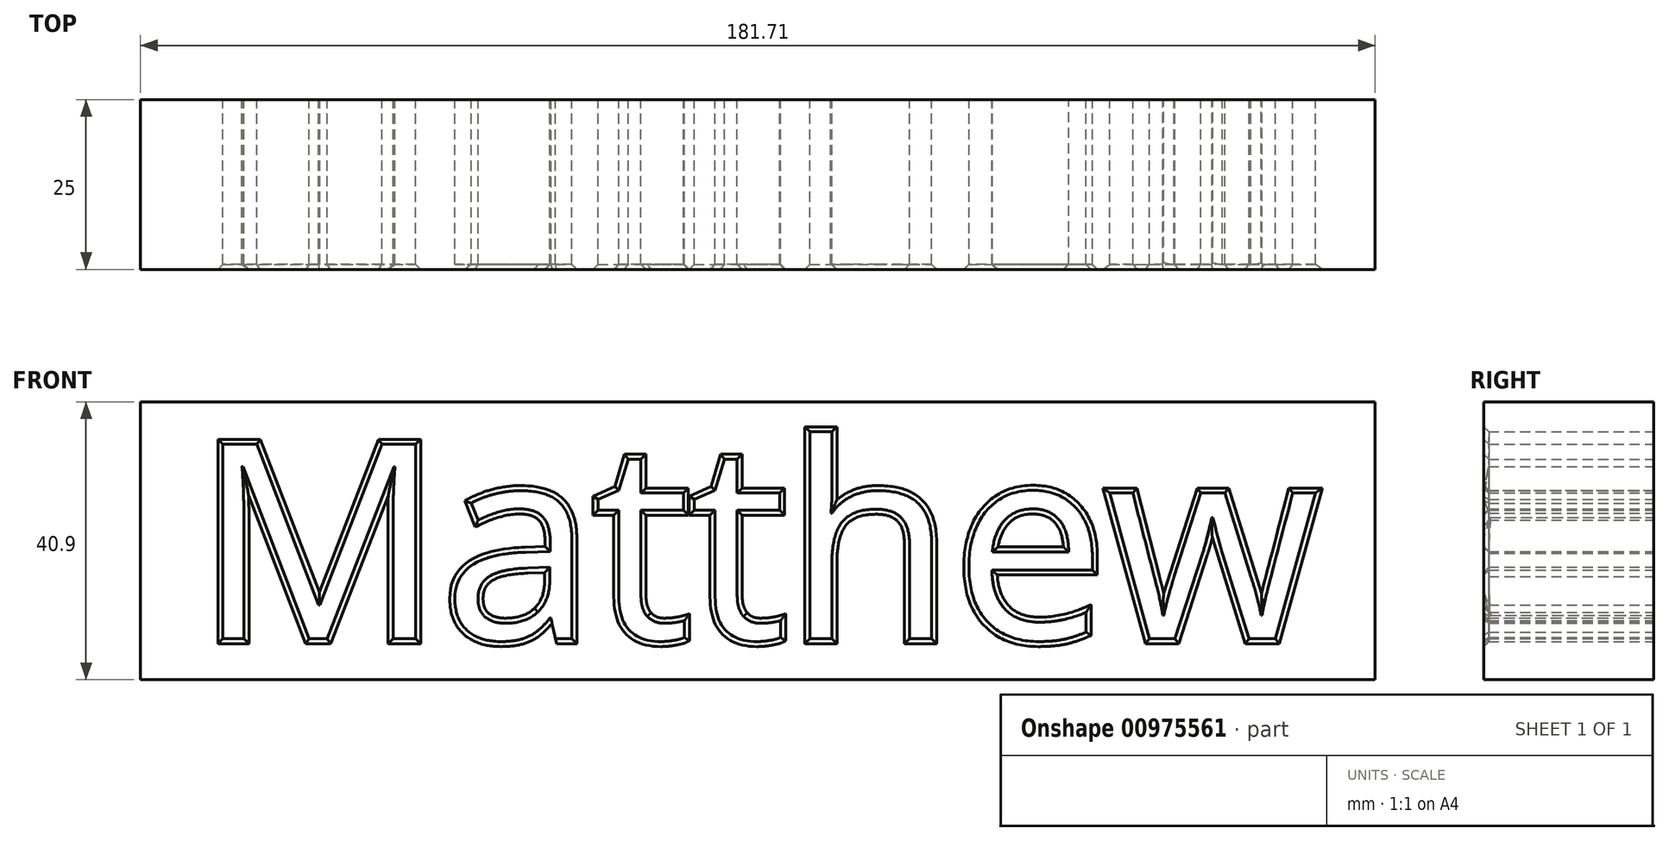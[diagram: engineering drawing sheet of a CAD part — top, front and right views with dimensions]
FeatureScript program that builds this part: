
annotation { "Feature Type Name" : "Feature", "Feature Type Description" : "" }
export const myFeature = defineFeature(function(context is Context, id is Id, definition is map)
    precondition{}
    {
        {
            var Q0;
            Q0=qCreatedBy(makeId("Front.planeOp"),FACE);
            var sketch = newSketch(context, id + "F0", { "sketchPlane" : qUnion([Q0])});
            skLineSegment(sketch, "E0.bottom", {"start": v(-90.14, 64.05) * mm, "end": v(91.57, 64.05) * mm});
            skLineSegment(sketch, "E0.top", {"start": v(-90.14, 23.15) * mm, "end": v(91.57, 23.15) * mm});
            skLineSegment(sketch, "E0.left", {"start": v(-90.14, 64.05) * mm, "end": v(-90.14, 23.15) * mm});
            skLineSegment(sketch, "E0.right", {"start": v(91.57, 64.05) * mm, "end": v(91.57, 23.15) * mm});
            skText(sketch, "E1", { "text": "Matthew", "fontName": "OpenSans-Regular.ttf"});
            const initialGuessF0  = {"E1": [-0.08195, 0.02915, 1, 0, 0.02889]};
            skSetInitialGuess(sketch, initialGuessF0);
            skSolve(sketch);
        }
        {
            var Q0;
            Q0=makeQuery(id+"F0.imprint","IMPRINT",FACE,{"disambiguationData":[TD([[makeQuery(id+"F0.imprint","IMPRINT",EDGE,{"derivedFrom":sQuery(id+"F0.wireOp",EDGE,"E0.bottom")}),-1.0]])]});
            var Q1;
            Q1=makeQuery(id+"F0.imprint","IMPRINT",FACE,{"disambiguationData":[TD([[makeQuery(id+"F0.imprint","IMPRINT",EDGE,{"derivedFrom":sQuery(id+"F0.wireOp",EDGE,"E1.sketch_text.stroke-37")}),1.0]])]});
            var Q2;
            Q2=makeQuery(id+"F0.imprint","IMPRINT",FACE,{"disambiguationData":[TD([[makeQuery(id+"F0.imprint","IMPRINT",EDGE,{"derivedFrom":sQuery(id+"F0.wireOp",EDGE,"E1.sketch_text.stroke-115")}),1.0]])]});
            extrude(context, id + "F1", {"entities" : qUnion([Q0, Q1, Q2]), "depth" : 25 * mm, "offsetDistance" : 25 * mm});
        }
        {
            var Q0;
            Q0=makeQuery(id+"F1.opExtrude","CAP_EDGE",EDGE,{"disambiguationData":[OSD([sQuery(id+"F0.wireOp",EDGE,"E1.sketch_text.stroke-7")])],"isStart":false});
            var Q1;
            Q1=makeQuery(id+"F1.opExtrude","CAP_EDGE",EDGE,{"disambiguationData":[OSD([sQuery(id+"F0.wireOp",EDGE,"E1.sketch_text.stroke-9")])],"isStart":false});
            var Q2;
            Q2=makeQuery(id+"F1.opExtrude","CAP_EDGE",EDGE,{"disambiguationData":[OSD([sQuery(id+"F0.wireOp",EDGE,"E1.sketch_text.stroke-16")])],"isStart":false});
            var Q3;
            Q3=makeQuery(id+"F1.opExtrude","CAP_EDGE",EDGE,{"disambiguationData":[OSD([sQuery(id+"F0.wireOp",EDGE,"E1.sketch_text.stroke-0")])],"isStart":false});
            var Q4;
            Q4=makeQuery(id+"F1.opExtrude","CAP_EDGE",EDGE,{"disambiguationData":[OSD([sQuery(id+"F0.wireOp",EDGE,"E1.sketch_text.stroke-6")])],"isStart":false});
            var Q5;
            Q5=makeQuery(id+"F1.opExtrude","CAP_EDGE",EDGE,{"disambiguationData":[OSD([sQuery(id+"F0.wireOp",EDGE,"E1.sketch_text.stroke-10")])],"isStart":false});
            var Q6;
            Q6=makeQuery(id+"F1.opExtrude","CAP_EDGE",EDGE,{"disambiguationData":[OSD([sQuery(id+"F0.wireOp",EDGE,"E1.sketch_text.stroke-11")])],"isStart":false});
            var Q7;
            Q7=makeQuery(id+"F1.opExtrude","CAP_EDGE",EDGE,{"disambiguationData":[OSD([sQuery(id+"F0.wireOp",EDGE,"E1.sketch_text.stroke-13")])],"isStart":false});
            var Q8;
            Q8=makeQuery(id+"F1.opExtrude","CAP_EDGE",EDGE,{"disambiguationData":[OSD([sQuery(id+"F0.wireOp",EDGE,"E1.sketch_text.stroke-3")])],"isStart":false});
            var Q9;
            Q9=makeQuery(id+"F1.opExtrude","CAP_EDGE",EDGE,{"disambiguationData":[OSD([sQuery(id+"F0.wireOp",EDGE,"E1.sketch_text.stroke-5")])],"isStart":false});
            var Q10;
            Q10=makeQuery(id+"F1.opExtrude","CAP_EDGE",EDGE,{"disambiguationData":[OSD([sQuery(id+"F0.wireOp",EDGE,"E1.sketch_text.stroke-2")])],"isStart":false});
            var Q11;
            Q11=makeQuery(id+"F1.opExtrude","CAP_EDGE",EDGE,{"disambiguationData":[OSD([sQuery(id+"F0.wireOp",EDGE,"E1.sketch_text.stroke-17")])],"isStart":false});
            var Q12;
            Q12=makeQuery(id+"F1.opExtrude","CAP_EDGE",EDGE,{"disambiguationData":[OSD([sQuery(id+"F0.wireOp",EDGE,"E1.sketch_text.stroke-4")])],"isStart":false});
            var Q13;
            Q13=makeQuery(id+"F1.opExtrude","CAP_EDGE",EDGE,{"disambiguationData":[OSD([sQuery(id+"F0.wireOp",EDGE,"E1.sketch_text.stroke-12")])],"isStart":false});
            var Q14;
            Q14=makeQuery(id+"F1.opExtrude","CAP_EDGE",EDGE,{"disambiguationData":[OSD([sQuery(id+"F0.wireOp",EDGE,"E1.sketch_text.stroke-14")])],"isStart":false});
            var Q15;
            Q15=makeQuery(id+"F1.opExtrude","CAP_EDGE",EDGE,{"disambiguationData":[OSD([sQuery(id+"F0.wireOp",EDGE,"E1.sketch_text.stroke-33")])],"isStart":false});
            var Q16;
            Q16=makeQuery(id+"F1.opExtrude","CAP_EDGE",EDGE,{"disambiguationData":[OSD([sQuery(id+"F0.wireOp",EDGE,"E1.sketch_text.stroke-24")])],"isStart":false});
            var Q17;
            Q17=makeQuery(id+"F1.opExtrude","CAP_EDGE",EDGE,{"disambiguationData":[OSD([sQuery(id+"F0.wireOp",EDGE,"E1.sketch_text.stroke-29")])],"isStart":false});
            var Q18;
            Q18=makeQuery(id+"F1.opExtrude","CAP_EDGE",EDGE,{"disambiguationData":[OSD([sQuery(id+"F0.wireOp",EDGE,"E1.sketch_text.stroke-30")])],"isStart":false});
            var Q19;
            Q19=makeQuery(id+"F1.opExtrude","CAP_EDGE",EDGE,{"disambiguationData":[OSD([sQuery(id+"F0.wireOp",EDGE,"E1.sketch_text.stroke-36")])],"isStart":false});
            var Q20;
            Q20=makeQuery(id+"F1.opExtrude","CAP_EDGE",EDGE,{"disambiguationData":[OSD([sQuery(id+"F0.wireOp",EDGE,"E1.sketch_text.stroke-41")])],"isStart":false});
            var Q21;
            Q21=makeQuery(id+"F1.opExtrude","CAP_EDGE",EDGE,{"disambiguationData":[OSD([sQuery(id+"F0.wireOp",EDGE,"E1.sketch_text.stroke-55")])],"isStart":false});
            var Q22;
            Q22=makeQuery(id+"F1.opExtrude","CAP_EDGE",EDGE,{"disambiguationData":[OSD([sQuery(id+"F0.wireOp",EDGE,"E1.sketch_text.stroke-56")])],"isStart":false});
            var Q23;
            Q23=makeQuery(id+"F1.opExtrude","CAP_EDGE",EDGE,{"disambiguationData":[OSD([sQuery(id+"F0.wireOp",EDGE,"E1.sketch_text.stroke-57")])],"isStart":false});
            var Q24;
            Q24=makeQuery(id+"F1.opExtrude","CAP_EDGE",EDGE,{"disambiguationData":[OSD([sQuery(id+"F0.wireOp",EDGE,"E1.sketch_text.stroke-58")])],"isStart":false});
            var Q25;
            Q25=makeQuery(id+"F1.opExtrude","CAP_EDGE",EDGE,{"disambiguationData":[OSD([sQuery(id+"F0.wireOp",EDGE,"E1.sketch_text.stroke-60")])],"isStart":false});
            var Q26;
            Q26=makeQuery(id+"F1.opExtrude","CAP_EDGE",EDGE,{"disambiguationData":[OSD([sQuery(id+"F0.wireOp",EDGE,"E1.sketch_text.stroke-59")])],"isStart":false});
            var Q27;
            Q27=makeQuery(id+"F1.opExtrude","CAP_EDGE",EDGE,{"disambiguationData":[OSD([sQuery(id+"F0.wireOp",EDGE,"E1.sketch_text.stroke-53")])],"isStart":false});
            var Q28;
            Q28=makeQuery(id+"F1.opExtrude","CAP_EDGE",EDGE,{"disambiguationData":[OSD([sQuery(id+"F0.wireOp",EDGE,"E1.sketch_text.stroke-54")])],"isStart":false});
            var Q29;
            Q29=makeQuery(id+"F1.opExtrude","CAP_EDGE",EDGE,{"disambiguationData":[OSD([sQuery(id+"F0.wireOp",EDGE,"E1.sketch_text.stroke-51")])],"isStart":false});
            var Q30;
            Q30=makeQuery(id+"F1.opExtrude","CAP_EDGE",EDGE,{"disambiguationData":[OSD([sQuery(id+"F0.wireOp",EDGE,"E1.sketch_text.stroke-52")])],"isStart":false});
            var Q31;
            Q31=makeQuery(id+"F1.opExtrude","CAP_EDGE",EDGE,{"disambiguationData":[OSD([sQuery(id+"F0.wireOp",EDGE,"E1.sketch_text.stroke-63")])],"isStart":false});
            var Q32;
            Q32=makeQuery(id+"F1.opExtrude","CAP_EDGE",EDGE,{"disambiguationData":[OSD([sQuery(id+"F0.wireOp",EDGE,"E1.sketch_text.stroke-47")])],"isStart":false});
            var Q33;
            Q33=makeQuery(id+"F1.opExtrude","CAP_EDGE",EDGE,{"disambiguationData":[OSD([sQuery(id+"F0.wireOp",EDGE,"E1.sketch_text.stroke-72")])],"isStart":false});
            var Q34;
            Q34=makeQuery(id+"F1.opExtrude","CAP_EDGE",EDGE,{"disambiguationData":[OSD([sQuery(id+"F0.wireOp",EDGE,"E1.sketch_text.stroke-73")])],"isStart":false});
            var Q35;
            Q35=makeQuery(id+"F1.opExtrude","CAP_EDGE",EDGE,{"disambiguationData":[OSD([sQuery(id+"F0.wireOp",EDGE,"E1.sketch_text.stroke-71")])],"isStart":false});
            var Q36;
            Q36=makeQuery(id+"F1.opExtrude","CAP_EDGE",EDGE,{"disambiguationData":[OSD([sQuery(id+"F0.wireOp",EDGE,"E1.sketch_text.stroke-70")])],"isStart":false});
            var Q37;
            Q37=makeQuery(id+"F1.opExtrude","CAP_EDGE",EDGE,{"disambiguationData":[OSD([sQuery(id+"F0.wireOp",EDGE,"E1.sketch_text.stroke-80")])],"isStart":false});
            var Q38;
            Q38=makeQuery(id+"F1.opExtrude","CAP_EDGE",EDGE,{"disambiguationData":[OSD([sQuery(id+"F0.wireOp",EDGE,"E1.sketch_text.stroke-66")])],"isStart":false});
            var Q39;
            Q39=makeQuery(id+"F1.opExtrude","CAP_EDGE",EDGE,{"disambiguationData":[OSD([sQuery(id+"F0.wireOp",EDGE,"E1.sketch_text.stroke-79")])],"isStart":false});
            var Q40;
            Q40=makeQuery(id+"F1.opExtrude","CAP_EDGE",EDGE,{"disambiguationData":[OSD([sQuery(id+"F0.wireOp",EDGE,"E1.sketch_text.stroke-78")])],"isStart":false});
            var Q41;
            Q41=makeQuery(id+"F1.opExtrude","CAP_EDGE",EDGE,{"disambiguationData":[OSD([sQuery(id+"F0.wireOp",EDGE,"E1.sketch_text.stroke-77")])],"isStart":false});
            var Q42;
            Q42=makeQuery(id+"F1.opExtrude","CAP_EDGE",EDGE,{"disambiguationData":[OSD([sQuery(id+"F0.wireOp",EDGE,"E1.sketch_text.stroke-76")])],"isStart":false});
            var Q43;
            Q43=makeQuery(id+"F1.opExtrude","CAP_EDGE",EDGE,{"disambiguationData":[OSD([sQuery(id+"F0.wireOp",EDGE,"E1.sketch_text.stroke-75")])],"isStart":false});
            var Q44;
            Q44=makeQuery(id+"F1.opExtrude","CAP_EDGE",EDGE,{"disambiguationData":[OSD([sQuery(id+"F0.wireOp",EDGE,"E1.sketch_text.stroke-74")])],"isStart":false});
            var Q45;
            Q45=makeQuery(id+"F1.opExtrude","CAP_EDGE",EDGE,{"disambiguationData":[OSD([sQuery(id+"F0.wireOp",EDGE,"E1.sketch_text.stroke-92")])],"isStart":false});
            var Q46;
            Q46=makeQuery(id+"F1.opExtrude","CAP_EDGE",EDGE,{"disambiguationData":[OSD([sQuery(id+"F0.wireOp",EDGE,"E1.sketch_text.stroke-93")])],"isStart":false});
            var Q47;
            Q47=makeQuery(id+"F1.opExtrude","CAP_EDGE",EDGE,{"disambiguationData":[OSD([sQuery(id+"F0.wireOp",EDGE,"E1.sketch_text.stroke-96")])],"isStart":false});
            var Q48;
            Q48=makeQuery(id+"F1.opExtrude","CAP_EDGE",EDGE,{"disambiguationData":[OSD([sQuery(id+"F0.wireOp",EDGE,"E1.sketch_text.stroke-100")])],"isStart":false});
            var Q49;
            Q49=makeQuery(id+"F1.opExtrude","CAP_EDGE",EDGE,{"disambiguationData":[OSD([sQuery(id+"F0.wireOp",EDGE,"E1.sketch_text.stroke-83")])],"isStart":false});
            var Q50;
            Q50=makeQuery(id+"F1.opExtrude","CAP_EDGE",EDGE,{"disambiguationData":[OSD([sQuery(id+"F0.wireOp",EDGE,"E1.sketch_text.stroke-89")])],"isStart":false});
            var Q51;
            Q51=makeQuery(id+"F1.opExtrude","CAP_EDGE",EDGE,{"disambiguationData":[OSD([sQuery(id+"F0.wireOp",EDGE,"E1.sketch_text.stroke-91")])],"isStart":false});
            var Q52;
            Q52=makeQuery(id+"F1.opExtrude","CAP_EDGE",EDGE,{"disambiguationData":[OSD([sQuery(id+"F0.wireOp",EDGE,"E1.sketch_text.stroke-90")])],"isStart":false});
            var Q53;
            Q53=makeQuery(id+"F1.opExtrude","CAP_EDGE",EDGE,{"disambiguationData":[OSD([sQuery(id+"F0.wireOp",EDGE,"E1.sketch_text.stroke-103")])],"isStart":false});
            var Q54;
            Q54=makeQuery(id+"F1.opExtrude","CAP_EDGE",EDGE,{"disambiguationData":[OSD([sQuery(id+"F0.wireOp",EDGE,"E1.sketch_text.stroke-108")])],"isStart":false});
            var Q55;
            Q55=makeQuery(id+"F1.opExtrude","CAP_EDGE",EDGE,{"disambiguationData":[OSD([sQuery(id+"F0.wireOp",EDGE,"E1.sketch_text.stroke-111")])],"isStart":false});
            var Q56;
            Q56=makeQuery(id+"F1.opExtrude","CAP_EDGE",EDGE,{"disambiguationData":[OSD([sQuery(id+"F0.wireOp",EDGE,"E1.sketch_text.stroke-112")])],"isStart":false});
            var Q57;
            Q57=makeQuery(id+"F1.opExtrude","CAP_EDGE",EDGE,{"disambiguationData":[OSD([sQuery(id+"F0.wireOp",EDGE,"E1.sketch_text.stroke-117")])],"isStart":false});
            var Q58;
            Q58=makeQuery(id+"F1.opExtrude","CAP_EDGE",EDGE,{"disambiguationData":[OSD([sQuery(id+"F0.wireOp",EDGE,"E1.sketch_text.stroke-119")])],"isStart":false});
            var Q59;
            Q59=makeQuery(id+"F1.opExtrude","CAP_EDGE",EDGE,{"disambiguationData":[OSD([sQuery(id+"F0.wireOp",EDGE,"E1.sketch_text.stroke-126")])],"isStart":false});
            var Q60;
            Q60=makeQuery(id+"F1.opExtrude","CAP_EDGE",EDGE,{"disambiguationData":[OSD([sQuery(id+"F0.wireOp",EDGE,"E1.sketch_text.stroke-128")])],"isStart":false});
            var Q61;
            Q61=makeQuery(id+"F1.opExtrude","CAP_EDGE",EDGE,{"disambiguationData":[OSD([sQuery(id+"F0.wireOp",EDGE,"E1.sketch_text.stroke-127")])],"isStart":false});
            var Q62;
            Q62=makeQuery(id+"F1.opExtrude","CAP_EDGE",EDGE,{"disambiguationData":[OSD([sQuery(id+"F0.wireOp",EDGE,"E1.sketch_text.stroke-125")])],"isStart":false});
            var Q63;
            Q63=makeQuery(id+"F1.opExtrude","CAP_EDGE",EDGE,{"disambiguationData":[OSD([sQuery(id+"F0.wireOp",EDGE,"E1.sketch_text.stroke-124")])],"isStart":false});
            var Q64;
            Q64=makeQuery(id+"F1.opExtrude","CAP_EDGE",EDGE,{"disambiguationData":[OSD([sQuery(id+"F0.wireOp",EDGE,"E1.sketch_text.stroke-133")])],"isStart":false});
            var Q65;
            Q65=makeQuery(id+"F1.opExtrude","CAP_EDGE",EDGE,{"disambiguationData":[OSD([sQuery(id+"F0.wireOp",EDGE,"E1.sketch_text.stroke-134")])],"isStart":false});
            var Q66;
            Q66=makeQuery(id+"F1.opExtrude","CAP_EDGE",EDGE,{"disambiguationData":[OSD([sQuery(id+"F0.wireOp",EDGE,"E1.sketch_text.stroke-135")])],"isStart":false});
            var Q67;
            Q67=makeQuery(id+"F1.opExtrude","CAP_EDGE",EDGE,{"disambiguationData":[OSD([sQuery(id+"F0.wireOp",EDGE,"E1.sketch_text.stroke-139")])],"isStart":false});
            var Q68;
            Q68=makeQuery(id+"F1.opExtrude","CAP_EDGE",EDGE,{"disambiguationData":[OSD([sQuery(id+"F0.wireOp",EDGE,"E1.sketch_text.stroke-140")])],"isStart":false});
            var Q69;
            Q69=makeQuery(id+"F1.opExtrude","CAP_EDGE",EDGE,{"disambiguationData":[OSD([sQuery(id+"F0.wireOp",EDGE,"E1.sketch_text.stroke-141")])],"isStart":false});
            var Q70;
            Q70=makeQuery(id+"F1.opExtrude","CAP_EDGE",EDGE,{"disambiguationData":[OSD([sQuery(id+"F0.wireOp",EDGE,"E1.sketch_text.stroke-142")])],"isStart":false});
            var Q71;
            Q71=makeQuery(id+"F1.opExtrude","CAP_EDGE",EDGE,{"disambiguationData":[OSD([sQuery(id+"F0.wireOp",EDGE,"E1.sketch_text.stroke-120")])],"isStart":false});
            chamfer(context, id + "F2", {"entities" : qUnion([Q0, Q1, Q2, Q3, Q4, Q5, Q6, Q7, Q8, Q9, Q10, Q11, Q12, Q13, Q14, Q15, Q16, Q17, Q18, Q19, Q20, Q21, Q22, Q23, Q24, Q25, Q26, Q27, Q28, Q29, Q30, Q31, Q32, Q33, Q34, Q35, Q36, Q37, Q38, Q39, Q40, Q41, Q42, Q43, Q44, Q45, Q46, Q47, Q48, Q49, Q50, Q51, Q52, Q53, Q54, Q55, Q56, Q57, Q58, Q59, Q60, Q61, Q62, Q63, Q64, Q65, Q66, Q67, Q68, Q69, Q70, Q71]), "width" : .75 * mm, "tangentPropagation" : true});
        }
    });
